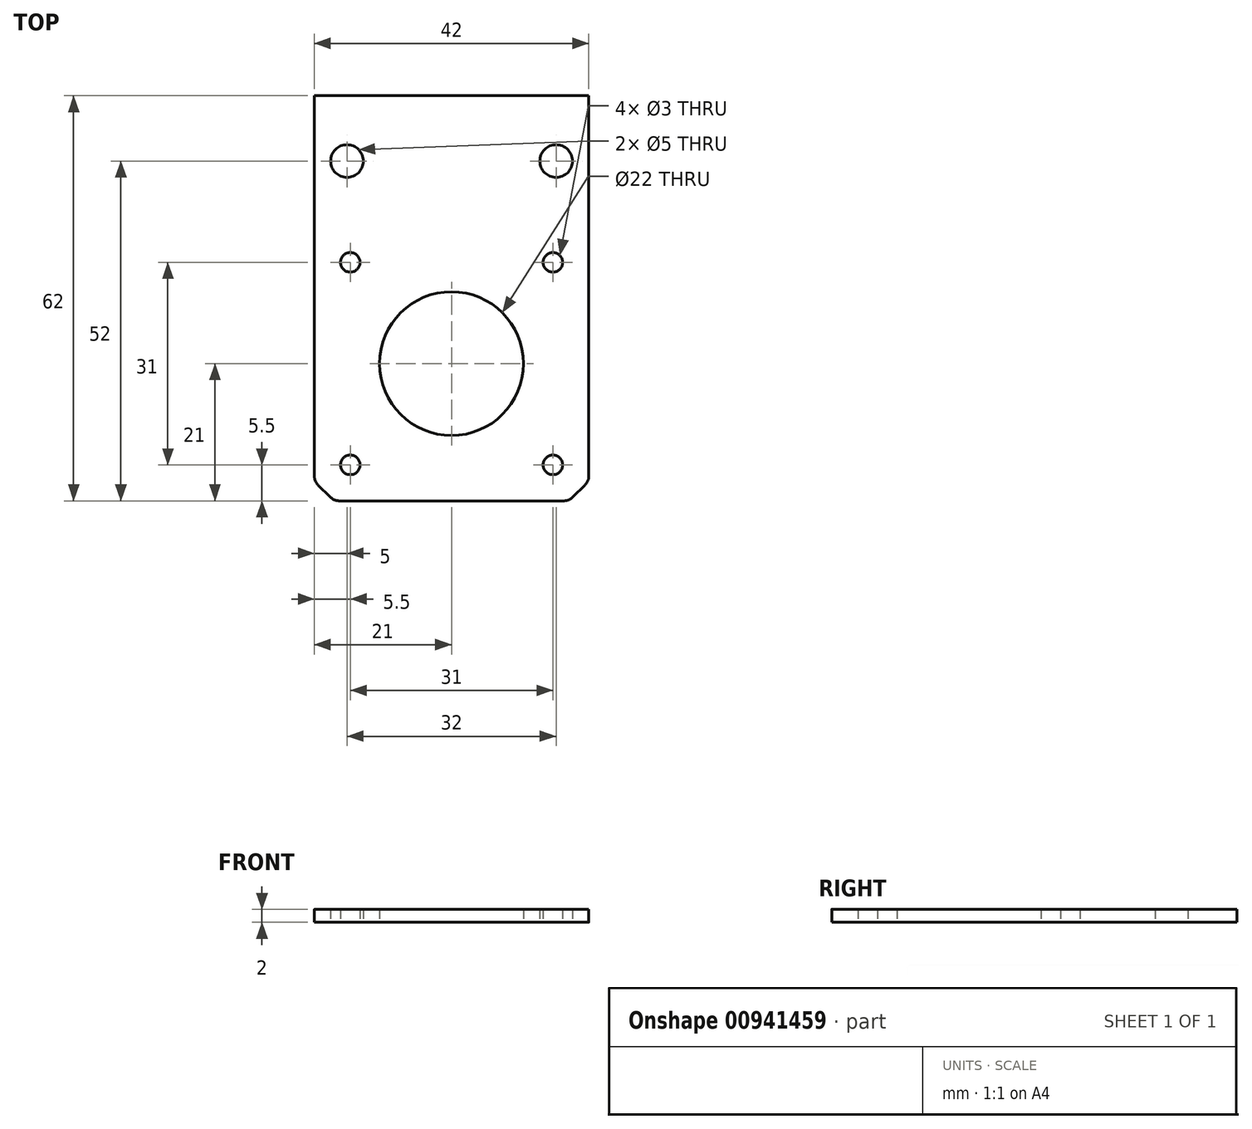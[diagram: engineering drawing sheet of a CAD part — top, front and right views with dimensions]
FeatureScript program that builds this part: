
annotation { "Feature Type Name" : "Feature", "Feature Type Description" : "" }
export const myFeature = defineFeature(function(context is Context, id is Id, definition is map)
    precondition{}
    {
        {
            var Q0;
            Q0=qCreatedBy(makeId("Top.planeOp"),FACE);
            var sketch = newSketch(context, id + "F0", { "sketchPlane" : qUnion([Q0])});
            skLineSegment(sketch, "E0.bottom", {"start": v(21, -31) * mm, "end": v(-21, -31) * mm});
            skLineSegment(sketch, "E0.top", {"start": v(21, 31) * mm, "end": v(-21, 31) * mm});
            skLineSegment(sketch, "E0.left", {"start": v(21, -31) * mm, "end": v(21, 31) * mm});
            skLineSegment(sketch, "E0.right", {"start": v(-21, -31) * mm, "end": v(-21, 31) * mm});
            skPoint(sketch, "E0.middle", {"position": v(0, 0) * mm});
            skCircle(sketch, "E1", {"center": v(-16, 21) * mm, "radius": 2.5 * mm});
            skCircle(sketch, "E2", {"center": v(16, 21) * mm, "radius": 2.5 * mm});
            skCircle(sketch, "E3", {"center": v(0, -10) * mm, "radius": 11 * mm});
            skCircle(sketch, "E4", {"center": v(15.5, -25.5) * mm, "radius": 1.5 * mm});
            skCircle(sketch, "E5", {"center": v(-15.5, -25.5) * mm, "radius": 1.5 * mm});
            skCircle(sketch, "E6", {"center": v(15.5, 5.5) * mm, "radius": 1.5 * mm});
            skCircle(sketch, "E7", {"center": v(-15.5, 5.5) * mm, "radius": 1.5 * mm});
            skSolve(sketch);
        }
        {
            var Q0;
            Q0=makeQuery(id+"F0.imprint","IMPRINT",FACE,{"disambiguationData":[TD([[makeQuery(id+"F0.imprint","IMPRINT",EDGE,{"derivedFrom":sQuery(id+"F0.wireOp",EDGE,"E0.bottom")}),-1.0]])]});
            extrude(context, id + "F1", {"entities" : qUnion([Q0]), "depth" : 2 * mm, "offsetDistance" : 25 * mm});
        }
        {
            var Q0;
            Q0=makeQuery(id+"F1.opExtrude","SWEPT_EDGE",EDGE,{"disambiguationData":[OSD([sQuery(id+"F0.wireOp",EDGE,"E0.bottom"),sQuery(id+"F0.wireOp",EDGE,"E0.right")])]});
            var Q1;
            Q1=makeQuery(id+"F1.opExtrude","SWEPT_EDGE",EDGE,{"disambiguationData":[OSD([sQuery(id+"F0.wireOp",EDGE,"E0.bottom"),sQuery(id+"F0.wireOp",EDGE,"E0.left")])]});
            chamfer(context, id + "F2", {"entities" : qUnion([Q0, Q1]), "width" : 3 * mm, "tangentPropagation" : true});
        }
        {
            var Q0;
            {var subQ0=sQuery(id+"F0.wireOp",EDGE,"E0.bottom");Q0=makeQuery(id+"F2.opChamfer","BLEND_EDGE",EDGE,{"blendedFrom":[makeQuery(id+"F1.opExtrude","SWEPT_EDGE",EDGE,{"disambiguationData":[OSD([subQ0,sQuery(id+"F0.wireOp",EDGE,"E0.right")])]}),makeQuery(id+"F1.opExtrude","SWEPT_FACE",FACE,{"disambiguationData":[OSD([subQ0])]})],"blendedInto":[makeQuery(id+"F1.opExtrude","SWEPT_FACE",FACE,{"disambiguationData":[OSD([subQ0])]})]});}
            var Q1;
            {var subQ0=sQuery(id+"F0.wireOp",EDGE,"E0.bottom");Q1=makeQuery(id+"F2.opChamfer","BLEND_EDGE",EDGE,{"blendedFrom":[makeQuery(id+"F1.opExtrude","SWEPT_EDGE",EDGE,{"disambiguationData":[OSD([subQ0,sQuery(id+"F0.wireOp",EDGE,"E0.left")])]}),makeQuery(id+"F1.opExtrude","SWEPT_FACE",FACE,{"disambiguationData":[OSD([subQ0])]})],"blendedInto":[makeQuery(id+"F1.opExtrude","SWEPT_FACE",FACE,{"disambiguationData":[OSD([subQ0])]})]});}
            var Q2;
            {var subQ0=sQuery(id+"F0.wireOp",EDGE,"E0.left");Q2=makeQuery(id+"F2.opChamfer","BLEND_EDGE",EDGE,{"blendedFrom":[makeQuery(id+"F1.opExtrude","SWEPT_EDGE",EDGE,{"disambiguationData":[OSD([sQuery(id+"F0.wireOp",EDGE,"E0.bottom"),subQ0])]}),makeQuery(id+"F1.opExtrude","SWEPT_FACE",FACE,{"disambiguationData":[OSD([subQ0])]})],"blendedInto":[makeQuery(id+"F1.opExtrude","SWEPT_FACE",FACE,{"disambiguationData":[OSD([subQ0])]})]});}
            var Q3;
            {var subQ0=sQuery(id+"F0.wireOp",EDGE,"E0.right");Q3=makeQuery(id+"F2.opChamfer","BLEND_EDGE",EDGE,{"blendedFrom":[makeQuery(id+"F1.opExtrude","SWEPT_EDGE",EDGE,{"disambiguationData":[OSD([sQuery(id+"F0.wireOp",EDGE,"E0.bottom"),subQ0])]}),makeQuery(id+"F1.opExtrude","SWEPT_FACE",FACE,{"disambiguationData":[OSD([subQ0])]})],"blendedInto":[makeQuery(id+"F1.opExtrude","SWEPT_FACE",FACE,{"disambiguationData":[OSD([subQ0])]})]});}
            fillet(context, id + "F3", {"entities" : qUnion([Q0, Q1, Q2, Q3]), "tangentPropagation" : true, "radius" : 2 * mm, "defaultsChanged" : true, "vertexSettings" : [], "allowEdgeOverflow" : false});
        }
    });
